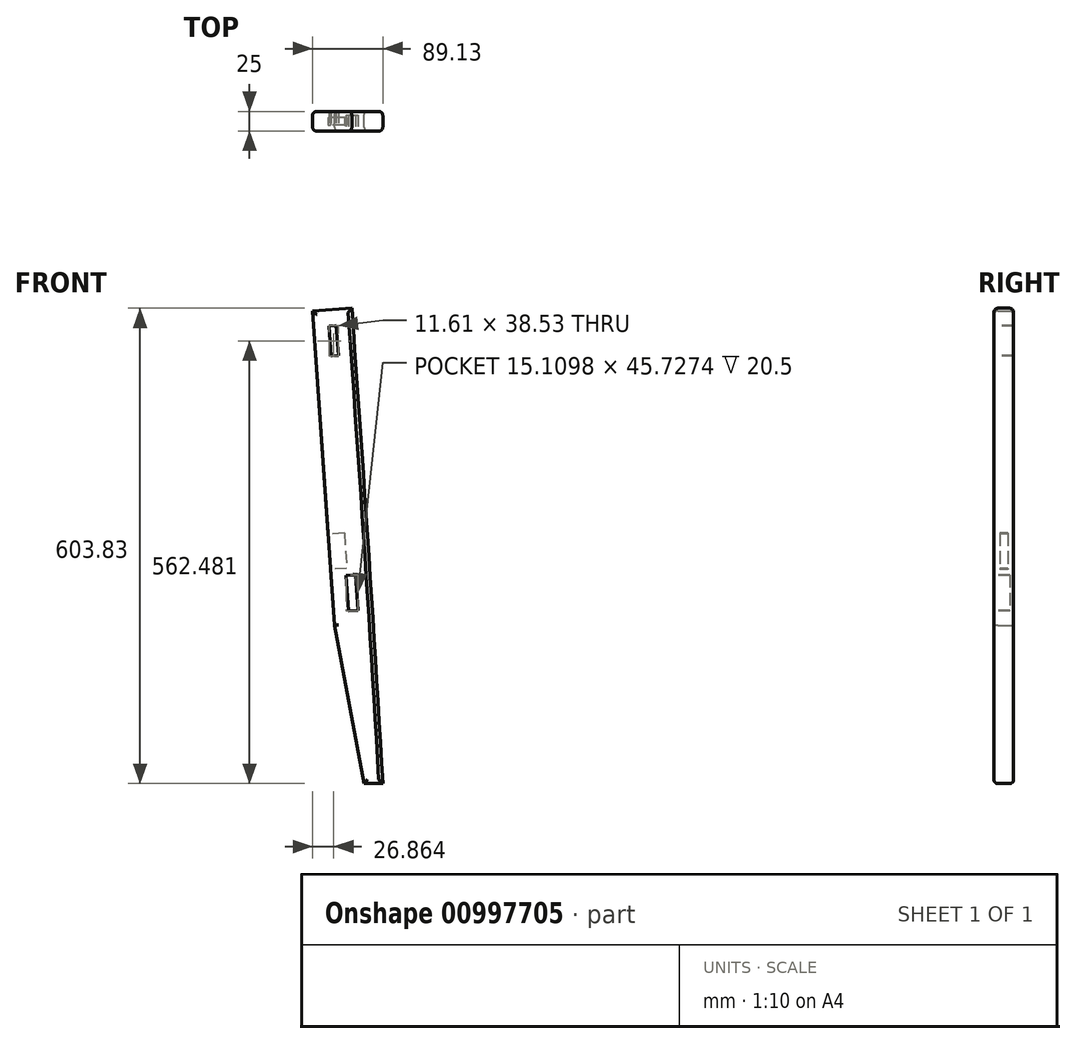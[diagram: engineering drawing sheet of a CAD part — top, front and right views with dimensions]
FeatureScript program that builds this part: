
annotation { "Feature Type Name" : "Feature", "Feature Type Description" : "" }
export const myFeature = defineFeature(function(context is Context, id is Id, definition is map)
    precondition{}
    {
        {
            var Q0;
            Q0=qCreatedBy(makeId("Front.planeOp"),FACE);
            var sketch = newSketch(context, id + "F0", { "sketchPlane" : qUnion([Q0])});
            skLineSegment(sketch, "E0", {"start": v(0, 600.34) * mm, "end": v(27.93, 200.94) * mm});
            skLineSegment(sketch, "E1", {"start": v(65.55, 0) * mm, "end": v(89.13, 0) * mm});
            skLineSegment(sketch, "E2", {"start": v(0, 600.34) * mm, "end": v(49.88, 603.83) * mm});
            skFitSpline(sketch, "E3", {"points": [v(49.88, 603.83) * mm, v(89.13, 0) * mm], "startDerivative": vector(41.98, -602.03) * mm, "endDerivative": vector(33.56, -602.83) * mm});
            skLineSegment(sketch, "E4", {"start": v(27.93, 200.94) * mm, "end": v(65.55, 0) * mm});
            skPoint(sketch, "E5.orphan", {"position": v(41.98, 0) * mm});
            skLineSegment(sketch, "E6.MirrorCS", {"start": v(0, 600.34) * mm, "end": v(-27.93, 200.94) * mm});
            skFitSpline(sketch, "E7.MirrorCS", {"points": [v(-49.88, 603.83) * mm, v(-89.13, 0) * mm], "startDerivative": vector(-41.98, -602.03) * mm, "endDerivative": vector(-33.56, -602.83) * mm});
            skLineSegment(sketch, "E8.MirrorCS", {"start": v(0, 600.34) * mm, "end": v(-49.88, 603.83) * mm});
            skLineSegment(sketch, "E9.MirrorCS", {"start": v(-27.93, 200.94) * mm, "end": v(-65.55, 0) * mm});
            skLineSegment(sketch, "E10.MirrorCS", {"start": v(-65.55, 0) * mm, "end": v(-89.13, 0) * mm});
            skSolve(sketch);
        }
        {
            var Q0;
            Q0=makeQuery(id+"F0.imprint","IMPRINT",FACE,{"disambiguationData":[TD([[makeQuery(id+"F0.imprint","IMPRINT",EDGE,{"derivedFrom":sQuery(id+"F0.wireOp",EDGE,"E0")}),1.0]])]});
            extrude(context, id + "F1", {"entities" : qUnion([Q0]), "depth" : 25 * mm, "offsetDistance" : 25 * mm});
        }
        {
            var Q0;
            Q0=makeQuery(id+"F1.opExtrude","CAP_FACE",FACE,{"disambiguationData":[OSD([sQuery(id+"F0.wireOp",EDGE,"E0"),sQuery(id+"F0.wireOp",EDGE,"E1"),sQuery(id+"F0.wireOp",EDGE,"E2"),sQuery(id+"F0.wireOp",EDGE,"E3"),sQuery(id+"F0.wireOp",EDGE,"E4")])],"isStart":false});
            fillet(context, id + "F2", {"entities" : qUnion([Q0]), "radius" : 5 * mm, "tangentPropagation" : true, "allowEdgeOverflow" : false});
        }
        {
            var Q0;
            Q0=makeQuery(id+"F1.opExtrude","CAP_FACE",FACE,{"disambiguationData":[OSD([sQuery(id+"F0.wireOp",EDGE,"E0"),sQuery(id+"F0.wireOp",EDGE,"E1"),sQuery(id+"F0.wireOp",EDGE,"E2"),sQuery(id+"F0.wireOp",EDGE,"E3"),sQuery(id+"F0.wireOp",EDGE,"E4")])],"isStart":true});
            fillet(context, id + "F3", {"entities" : qUnion([Q0]), "radius" : 5 * mm, "tangentPropagation" : true, "allowEdgeOverflow" : false});
        }
        {
            var Q0;
            Q0=makeQuery(id+"F1.opExtrude","SWEPT_FACE",FACE,{"disambiguationData":[OSD([sQuery(id+"F0.wireOp",EDGE,"E0")])]});
            var sketch = newSketch(context, id + "F4", { "sketchPlane" : qUnion([Q0])});
            skLineSegment(sketch, "E11.bottom", {"start": v(7.51, 314.7) * mm, "end": v(17.51, 314.7) * mm});
            skLineSegment(sketch, "E11.top", {"start": v(7.51, 269.7) * mm, "end": v(17.51, 269.7) * mm});
            skLineSegment(sketch, "E11.left", {"start": v(7.51, 314.7) * mm, "end": v(7.51, 269.7) * mm});
            skLineSegment(sketch, "E11.right", {"start": v(17.51, 314.7) * mm, "end": v(17.51, 269.7) * mm});
            skPoint(sketch, "E11.middle", {"position": v(12.51, 292.2) * mm});
            skSolve(sketch);
        }
        {
            var Q0;
            Q0=makeQuery(id+"F4.imprint","IMPRINT",FACE,{"disambiguationData":[TD([[makeQuery(id+"F4.imprint","IMPRINT",EDGE,{"derivedFrom":sQuery(id+"F4.wireOp",EDGE,"E11.bottom")}),-1.0]])]});
            extrude(context, id + "F5", {"entities" : qUnion([Q0]), "operationType" : NewBodyOperationType.REMOVE, "oppositeDirection" : true, "depth" : 20.5 * mm, "offsetDistance" : 25 * mm});
        }
        {
            var Q0;
            Q0=makeQuery(id+"F1.opExtrude","CAP_FACE",FACE,{"disambiguationData":[OSD([sQuery(id+"F0.wireOp",EDGE,"E0"),sQuery(id+"F0.wireOp",EDGE,"E1"),sQuery(id+"F0.wireOp",EDGE,"E2"),sQuery(id+"F0.wireOp",EDGE,"E3"),sQuery(id+"F0.wireOp",EDGE,"E4")])],"isStart":false});
            var sketch = newSketch(context, id + "F6", { "sketchPlane" : qUnion([Q0])});
            skLineSegment(sketch, "E12.bottom", {"start": v(42.44, 264.23) * mm, "end": v(54.42, 265.07) * mm});
            skLineSegment(sketch, "E12.top", {"start": v(45.58, 219.34) * mm, "end": v(57.55, 220.17) * mm});
            skLineSegment(sketch, "E12.left", {"start": v(42.44, 264.23) * mm, "end": v(45.58, 219.34) * mm});
            skLineSegment(sketch, "E12.right", {"start": v(54.42, 265.07) * mm, "end": v(57.55, 220.17) * mm});
            skPoint(sketch, "E12.middle", {"position": v(50, 242.2) * mm});
            skSolve(sketch);
        }
        {
            var Q0;
            Q0=makeQuery(id+"F6.imprint","IMPRINT",FACE,{"disambiguationData":[TD([[makeQuery(id+"F6.imprint","IMPRINT",EDGE,{"derivedFrom":sQuery(id+"F6.wireOp",EDGE,"E12.bottom")}),-1.0]])]});
            extrude(context, id + "F7", {"entities" : qUnion([Q0]), "operationType" : NewBodyOperationType.REMOVE, "oppositeDirection" : true, "depth" : 20.5 * mm, "offsetDistance" : 25 * mm});
        }
        {
            var Q0;
            Q0=makeQuery(id+"F1.opExtrude","CAP_FACE",FACE,{"disambiguationData":[OSD([sQuery(id+"F0.wireOp",EDGE,"E0"),sQuery(id+"F0.wireOp",EDGE,"E1"),sQuery(id+"F0.wireOp",EDGE,"E2"),sQuery(id+"F0.wireOp",EDGE,"E3"),sQuery(id+"F0.wireOp",EDGE,"E4")])],"isStart":false});
            var sketch = newSketch(context, id + "F8", { "sketchPlane" : qUnion([Q0])});
            skLineSegment(sketch, "E13.top", {"start": v(23.71, 543.21) * mm, "end": v(32.67, 543.84) * mm});
            skLineSegment(sketch, "E13.left", {"start": v(21.06, 581.12) * mm, "end": v(23.71, 543.21) * mm});
            skLineSegment(sketch, "E13.right", {"start": v(30.06, 581.12) * mm, "end": v(32.67, 543.84) * mm});
            skPoint(sketch, "E13.middle", {"position": v(28.21, 562.21) * mm});
            skLineSegment(sketch, "E14", {"start": v(21.06, 581.12) * mm, "end": v(30.02, 581.75) * mm});
            skLineSegment(sketch, "E15", {"start": v(30.06, 581.12) * mm, "end": v(30.02, 581.75) * mm});
            skPoint(sketch, "E16.orphan", {"position": v(30.04, 581.75) * mm});
            skPoint(sketch, "E17.orphan", {"position": v(30.02, 581.75) * mm});
            skSolve(sketch);
        }
        {
            var Q0;
            Q0 = qSketchRegion(id + "F8", true);
            extrude(context, id + "F9", {"entities" : qUnion([Q0]), "operationType" : NewBodyOperationType.REMOVE, "oppositeDirection" : true, "depth" : 25.5 * mm, "offsetDistance" : 25 * mm});
        }
        {
            var Q0;
            Q0 = qSketchRegion(id + "F8", true);
            extrude(context, id + "F10", {"entities" : qUnion([Q0]), "operationType" : NewBodyOperationType.REMOVE, "oppositeDirection" : true, "depth" : 25 * mm, "offsetDistance" : 25 * mm});
        }
        {
            var Q0;
            Q0 = qSketchRegion(id + "F8", true);
            extrude(context, id + "F11", {"entities" : qUnion([Q0]), "operationType" : NewBodyOperationType.REMOVE, "oppositeDirection" : true, "depth" : 25.5 * mm, "offsetDistance" : 25 * mm});
        }
    });
